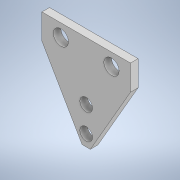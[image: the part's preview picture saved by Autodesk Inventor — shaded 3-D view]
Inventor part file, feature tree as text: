
AUTODESK INVENTOR PART (.ipt)
format: ipt  version: 2022 (Build 260153000, 153)  size: 132,608 bytes
history: native  units: mm
features: plane x7, extrude x1, mirror x1, sketch x1
ambient origin geometry x8: Origin, YZ Plane, XZ Plane, XY Plane, X Axis, Y Axis, Z Axis, Center Point
bodies: Solid1 (feature_tree)
feature tree (10):
  extrude  "Extrusion1"  Depth=10.0mm
  plane  "Work Plane4"
  mirror  "Mirror1"
  plane  "Work Plane10"
  plane  "Work Plane12"
  sketch  "Sketch1"  dims[d1=5.0mm d2=10.0mm d3=6.0mm d4=10.0mm d5=60.0deg d10=35.0mm d11=17.5mm d13=3.258248mm d17=120.0deg d18=3.0mm d19=0.0mm d20=10.0mm d22=23.0mm d25=-5.0mm d26=5.0mm]
  plane  "Work Plane1"
  plane  "Work Plane3"
  plane  "Work Plane5"
  plane  "Work Plane11"
